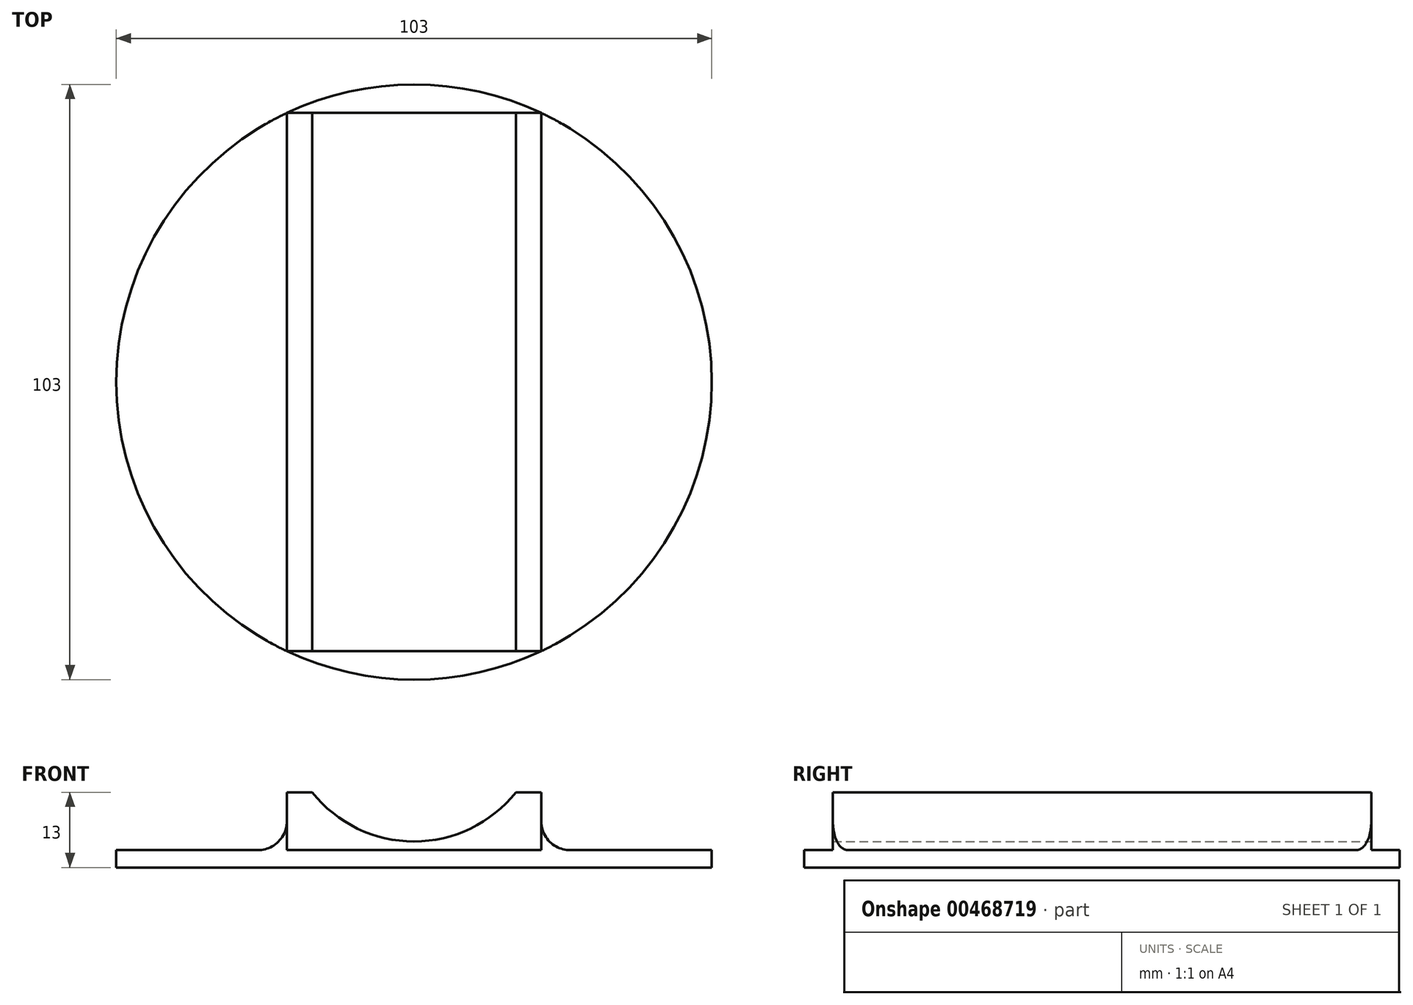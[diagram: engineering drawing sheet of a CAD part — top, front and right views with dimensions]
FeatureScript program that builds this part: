
annotation { "Feature Type Name" : "Feature", "Feature Type Description" : "" }
export const myFeature = defineFeature(function(context is Context, id is Id, definition is map)
    precondition{}
    {
        {
            var Q0;
            Q0=qCreatedBy(makeId("Top.planeOp"),FACE);
            var sketch = newSketch(context, id + "F0", { "sketchPlane" : qUnion([Q0])});
            skCircle(sketch, "E0", {"center": v(0, 0) * mm, "radius": 51.5 * mm});
            skSolve(sketch);
        }
        {
            var Q0;
            Q0=makeQuery(id+"F0.imprint","IMPRINT",FACE,{"disambiguationData":[TD([[makeQuery(id+"F0.imprint","IMPRINT",EDGE,{"derivedFrom":sQuery(id+"F0.wireOp",EDGE,"E0")}),1.0]])]});
            extrude(context, id + "F1", {"entities" : qUnion([Q0]), "depth" : 3 * mm});
        }
        {
            var Q0;
            Q0=makeQuery(id+"F1.opExtrude","CAP_FACE",FACE,{"disambiguationData":[OSD([sQuery(id+"F0.wireOp",EDGE,"E0")])],"isStart":false});
            var sketch = newSketch(context, id + "F2", { "sketchPlane" : qUnion([Q0])});
            skLineSegment(sketch, "E1.bottom", {"start": v(22, 46.56) * mm, "end": v(-22, 46.56) * mm});
            skLineSegment(sketch, "E1.top", {"start": v(22, -46.56) * mm, "end": v(-22, -46.56) * mm});
            skLineSegment(sketch, "E1.left", {"start": v(22, 46.56) * mm, "end": v(22, -46.56) * mm});
            skLineSegment(sketch, "E1.right", {"start": v(-22, 46.56) * mm, "end": v(-22, -46.56) * mm});
            skSolve(sketch);
        }
        {
            var Q0;
            Q0=makeQuery(id+"F2.imprint","IMPRINT",FACE,{"disambiguationData":[TD([[makeQuery(id+"F2.imprint","IMPRINT",EDGE,{"derivedFrom":sQuery(id+"F2.wireOp",EDGE,"E1.bottom")}),1.0]])]});
            extrude(context, id + "F3", {"entities" : qUnion([Q0]), "operationType" : NewBodyOperationType.ADD, "depth" : 10 * mm});
        }
        {
            var Q0;
            Q0=makeQuery(id+"F3.opExtrude","SWEPT_FACE",FACE,{"disambiguationData":[OSD([sQuery(id+"F2.wireOp",EDGE,"E1.bottom")])]});
            var sketch = newSketch(context, id + "F4", { "sketchPlane" : qUnion([Q0])});
            skCircle(sketch, "E2", {"center": v(0, 27) * mm, "radius": 22.5 * mm});
            skSolve(sketch);
        }
        {
            var Q0;
            {var subQ0=sQuery(id+"F4.wireOp",EDGE,"E2");var subQ1=makeQuery(id+"F3.opExtrude","CAP_EDGE",EDGE,{"disambiguationData":[OSD([sQuery(id+"F2.wireOp",EDGE,"E1.bottom")])],"isStart":false});var subQ2=makeQuery(id+"F4.imprint","INTERSECT",VERTEX,{"disambiguationData":[OD(0.0)],"derivedFrom":[subQ1,subQ0]});Q0=makeQuery(id+"F4.imprint","IMPRINT",FACE,{"disambiguationData":[TD([[makeQuery(id+"F4.imprint","IMPRINT",EDGE,{"disambiguationData":[TD([[subQ2,-1.0]])],"derivedFrom":subQ0}),1.0]])]});}
            var Q1;
            Q1=sQuery(id+"F4.wireOp",EDGE,"E2");
            extrude(context, id + "F5", {"entities" : qUnion([Q0]), "operationType" : NewBodyOperationType.REMOVE, "surfaceEntities" : qUnion([Q1]), "endBound" : BoundingType.UP_TO_NEXT, "oppositeDirection" : true, "depth" : 25 * mm});
        }
        {
            var Q0;
            Q0=makeQuery(id+"F3.opExtrude","CAP_EDGE",EDGE,{"disambiguationData":[OSD([sQuery(id+"F2.wireOp",EDGE,"E1.right")])],"isStart":true});
            fillet(context, id + "F6", {"entities" : qUnion([Q0]), "radius" : 5 * mm, "tangentPropagation" : true, "allowEdgeOverflow" : false});
        }
        {
            var Q0;
            Q0=makeQuery(id+"F3.opExtrude","CAP_EDGE",EDGE,{"disambiguationData":[OSD([sQuery(id+"F2.wireOp",EDGE,"E1.left")])],"isStart":true});
            fillet(context, id + "F7", {"entities" : qUnion([Q0]), "radius" : 5 * mm, "tangentPropagation" : true, "allowEdgeOverflow" : false});
        }
    });
